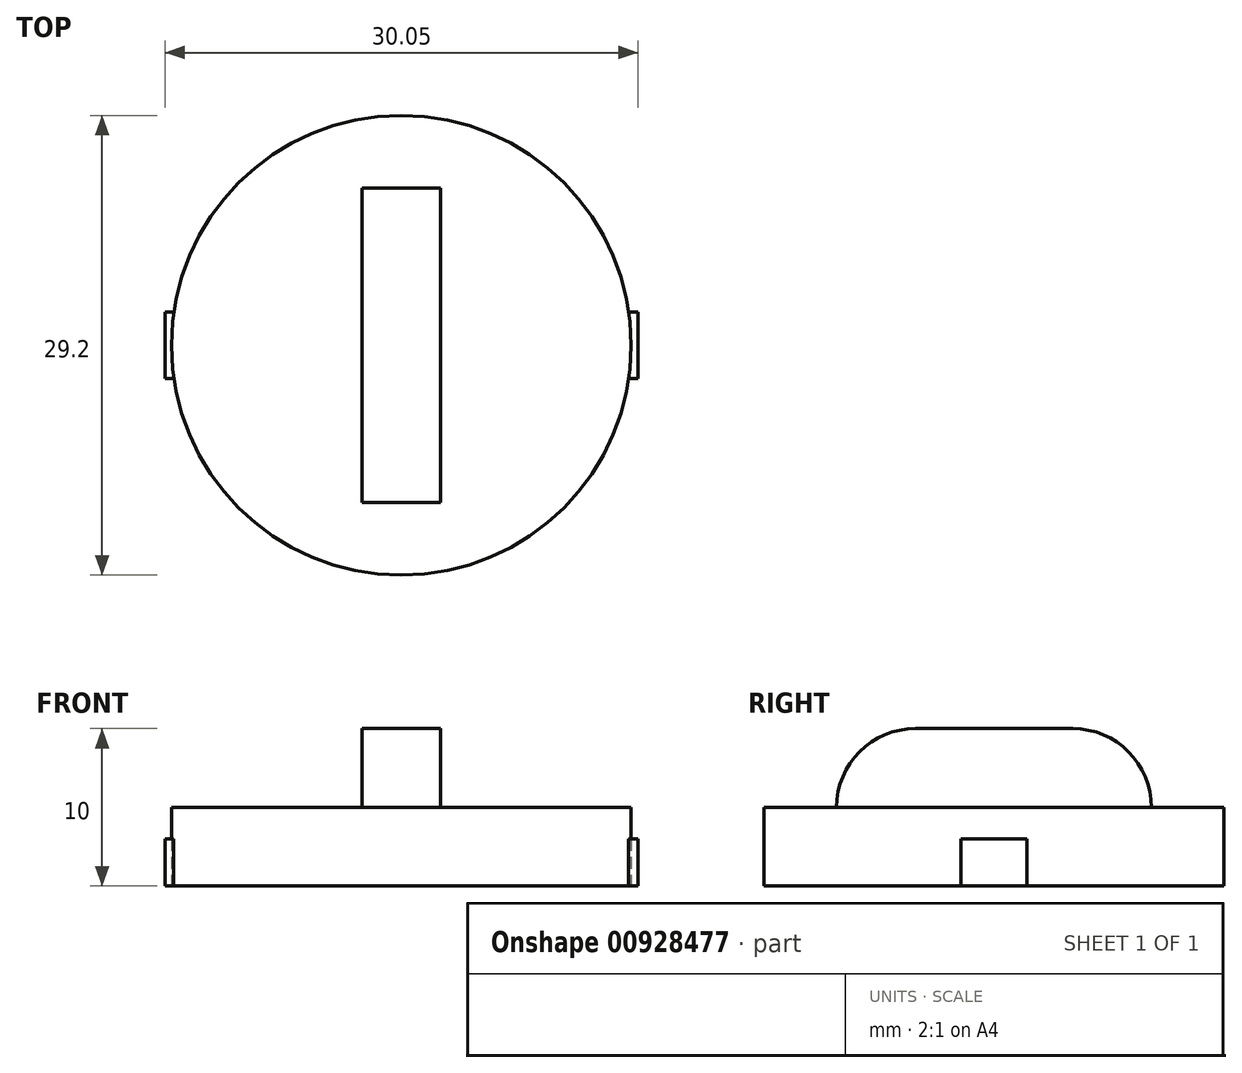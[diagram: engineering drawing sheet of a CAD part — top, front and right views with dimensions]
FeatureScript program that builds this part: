
annotation { "Feature Type Name" : "Feature", "Feature Type Description" : "" }
export const myFeature = defineFeature(function(context is Context, id is Id, definition is map)
    precondition{}
    {
        {
            var Q0;
            Q0=qCreatedBy(makeId("Top.planeOp"),FACE);
            var sketch = newSketch(context, id + "F0", { "sketchPlane" : qUnion([Q0])});
            skCircle(sketch, "E0", {"center": v(0, 0) * mm, "radius": 14.6 * mm});
            skLineSegment(sketch, "E1.bottom", {"start": v(14.45, 2.1) * mm, "end": v(15.05, 2.1) * mm});
            skLineSegment(sketch, "E1.top", {"start": v(14.45, -2.1) * mm, "end": v(15.05, -2.1) * mm});
            skLineSegment(sketch, "E1.left", {"start": v(14.45, 2.1) * mm, "end": v(14.45, -2.1) * mm});
            skLineSegment(sketch, "E1.right", {"start": v(15.05, 2.1) * mm, "end": v(15.05, -2.1) * mm});
            skLineSegment(sketch, "E2.bottom", {"start": v(-15, 2.1) * mm, "end": v(-14.4, 2.1) * mm});
            skLineSegment(sketch, "E2.top", {"start": v(-15, -2.1) * mm, "end": v(-14.4, -2.1) * mm});
            skLineSegment(sketch, "E2.left", {"start": v(-15, 2.1) * mm, "end": v(-15, -2.1) * mm});
            skLineSegment(sketch, "E2.right", {"start": v(-14.4, 2.1) * mm, "end": v(-14.4, -2.1) * mm});
            skLineSegment(sketch, "E3.bottom", {"start": v(-2.5, 10) * mm, "end": v(2.5, 10) * mm});
            skLineSegment(sketch, "E3.top", {"start": v(-2.5, -10) * mm, "end": v(2.5, -10) * mm});
            skLineSegment(sketch, "E3.left", {"start": v(-2.5, 10) * mm, "end": v(-2.5, -10) * mm});
            skLineSegment(sketch, "E3.right", {"start": v(2.5, 10) * mm, "end": v(2.5, -10) * mm});
            skSolve(sketch);
        }
        {
            var Q0;
            {var subQ4=sQuery(id+"F0.wireOp",EDGE,"E1.left");Q0=makeQuery(id+"F0.imprint","IMPRINT",FACE,{"disambiguationData":[TD([[makeQuery(id+"F0.imprint","IMPRINT",EDGE,{"derivedFrom":subQ4}),-1.0]])]});}
            var Q1;
            {var subQ0=sQuery(id+"F0.wireOp",EDGE,"E1.left");Q1=makeQuery(id+"F0.imprint","IMPRINT",FACE,{"disambiguationData":[TD([[makeQuery(id+"F0.imprint","IMPRINT",EDGE,{"derivedFrom":subQ0}),1.0]])]});}
            var Q2;
            {var subQ5=sQuery(id+"F0.wireOp",EDGE,"E2.right");Q2=makeQuery(id+"F0.imprint","IMPRINT",FACE,{"disambiguationData":[TD([[makeQuery(id+"F0.imprint","IMPRINT",EDGE,{"derivedFrom":subQ5}),-1.0]])]});}
            extrude(context, id + "F1", {"entities" : qUnion([Q0, Q1, Q2]), "depth" : 5 * mm, "offsetDistance" : 25 * mm});
        }
        {
            var Q0;
            {var subQ5=sQuery(id+"F0.wireOp",EDGE,"E2.left");Q0=makeQuery(id+"F0.imprint","IMPRINT",FACE,{"disambiguationData":[TD([[makeQuery(id+"F0.imprint","IMPRINT",EDGE,{"derivedFrom":subQ5}),1.0]])]});}
            var Q1;
            {var subQ1=sQuery(id+"F0.wireOp",EDGE,"E1.bottom");Q1=makeQuery(id+"F0.imprint","IMPRINT",FACE,{"disambiguationData":[TD([[makeQuery(id+"F0.imprint","IMPRINT",EDGE,{"derivedFrom":subQ1}),-1.0]])]});}
            extrude(context, id + "F2", {"entities" : qUnion([Q0, Q1]), "depth" : 3 * mm, "offsetDistance" : 25 * mm});
        }
        {
            var Q0;
            Q0=makeQuery(id+"F0.imprint","IMPRINT",FACE,{"disambiguationData":[TD([[makeQuery(id+"F0.imprint","IMPRINT",EDGE,{"derivedFrom":sQuery(id+"F0.wireOp",EDGE,"E3.bottom")}),-1.0]])]});
            extrude(context, id + "F3", {"entities" : qUnion([Q0]), "operationType" : NewBodyOperationType.ADD, "depth" : 10 * mm, "offsetDistance" : 25 * mm});
        }
        {
            var Q0;
            Q0=makeQuery(id+"F3.opExtrude","CAP_EDGE",EDGE,{"disambiguationData":[OSD([sQuery(id+"F0.wireOp",EDGE,"E3.bottom")])],"isStart":false});
            var Q1;
            Q1=makeQuery(id+"F3.opExtrude","CAP_EDGE",EDGE,{"disambiguationData":[OSD([sQuery(id+"F0.wireOp",EDGE,"E3.top")])],"isStart":false});
            fillet(context, id + "F4", {"entities" : qUnion([Q0, Q1]), "radius" : 5 * mm, "tangentPropagation" : true, "allowEdgeOverflow" : false});
        }
    });
